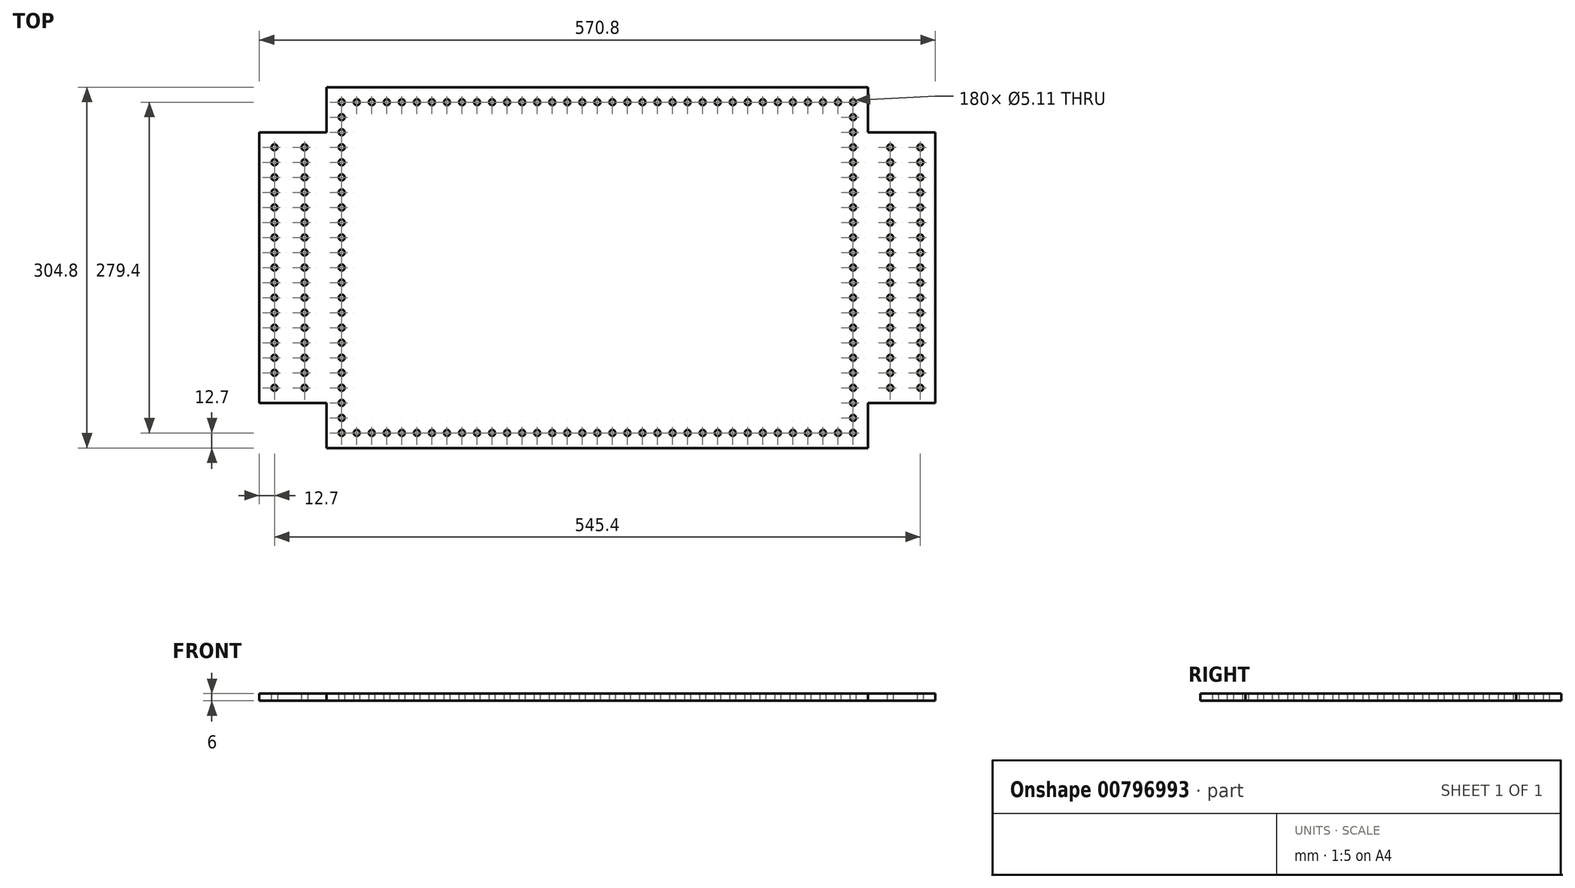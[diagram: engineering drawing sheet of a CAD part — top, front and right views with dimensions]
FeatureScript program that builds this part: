
annotation { "Feature Type Name" : "Feature", "Feature Type Description" : "" }
export const myFeature = defineFeature(function(context is Context, id is Id, definition is map)
    precondition{}
    {
        {
            var Q0;
            Q0=qCreatedBy(makeId("Top.planeOp"),FACE);
            var sketch = newSketch(context, id + "F0", { "sketchPlane" : qUnion([Q0])});
            skLineSegment(sketch, "E0.bottom", {"start": v(228.6, 152.4) * mm, "end": v(-228.6, 152.4) * mm});
            skLineSegment(sketch, "E0.top", {"start": v(228.6, -152.4) * mm, "end": v(-228.6, -152.4) * mm});
            skLineSegment(sketch, "E0.left", {"start": v(228.6, 152.4) * mm, "end": v(228.6, -152.4) * mm, "construction": true});
            skLineSegment(sketch, "E0.right", {"start": v(-228.6, 152.4) * mm, "end": v(-228.6, -152.4) * mm, "construction": true});
            skCircle(sketch, "E1", {"center": v(-215.9, 139.7) * mm, "radius": 2.55 * mm});
            skCircle(sketch, "E2.0.1.0", {"center": v(-215.9, 127) * mm, "radius": 2.55 * mm});
            skCircle(sketch, "E2.0.2.0", {"center": v(-215.9, 114.3) * mm, "radius": 2.55 * mm});
            skCircle(sketch, "E2.0.3.0", {"center": v(-215.9, 101.6) * mm, "radius": 2.55 * mm});
            skCircle(sketch, "E2.0.4.0", {"center": v(-215.9, 88.9) * mm, "radius": 2.55 * mm});
            skCircle(sketch, "E2.0.5.0", {"center": v(-215.9, 76.2) * mm, "radius": 2.55 * mm});
            skCircle(sketch, "E2.0.6.0", {"center": v(-215.9, 63.5) * mm, "radius": 2.55 * mm});
            skCircle(sketch, "E2.0.7.0", {"center": v(-215.9, 50.8) * mm, "radius": 2.55 * mm});
            skCircle(sketch, "E2.0.8.0", {"center": v(-215.9, 38.1) * mm, "radius": 2.55 * mm});
            skCircle(sketch, "E2.0.9.0", {"center": v(-215.9, 25.4) * mm, "radius": 2.55 * mm});
            skCircle(sketch, "E2.0.10.0", {"center": v(-215.9, 12.7) * mm, "radius": 2.55 * mm});
            skCircle(sketch, "E2.0.11.0", {"center": v(-215.9, 0) * mm, "radius": 2.55 * mm});
            skCircle(sketch, "E2.0.12.0", {"center": v(-215.9, -12.7) * mm, "radius": 2.55 * mm});
            skCircle(sketch, "E2.0.13.0", {"center": v(-215.9, -25.4) * mm, "radius": 2.55 * mm});
            skCircle(sketch, "E2.0.14.0", {"center": v(-215.9, -38.1) * mm, "radius": 2.55 * mm});
            skCircle(sketch, "E2.0.15.0", {"center": v(-215.9, -50.8) * mm, "radius": 2.55 * mm});
            skCircle(sketch, "E2.0.16.0", {"center": v(-215.9, -63.5) * mm, "radius": 2.55 * mm});
            skCircle(sketch, "E2.0.17.0", {"center": v(-215.9, -76.2) * mm, "radius": 2.55 * mm});
            skCircle(sketch, "E2.0.18.0", {"center": v(-215.9, -88.9) * mm, "radius": 2.55 * mm});
            skCircle(sketch, "E2.0.19.0", {"center": v(-215.9, -101.6) * mm, "radius": 2.55 * mm});
            skCircle(sketch, "E2.0.20.0", {"center": v(-215.9, -114.3) * mm, "radius": 2.55 * mm});
            skCircle(sketch, "E2.0.21.0", {"center": v(-215.9, -127) * mm, "radius": 2.55 * mm});
            skCircle(sketch, "E2.0.22.0", {"center": v(-215.9, -139.7) * mm, "radius": 2.55 * mm});
            skCircle(sketch, "E2.1.0.0", {"center": v(-203.2, 139.7) * mm, "radius": 2.55 * mm});
            skCircle(sketch, "E2.1.22.0", {"center": v(-203.2, -139.7) * mm, "radius": 2.55 * mm});
            skCircle(sketch, "E2.2.0.0", {"center": v(-190.5, 139.7) * mm, "radius": 2.55 * mm});
            skCircle(sketch, "E2.2.22.0", {"center": v(-190.5, -139.7) * mm, "radius": 2.55 * mm});
            skCircle(sketch, "E2.3.0.0", {"center": v(-177.8, 139.7) * mm, "radius": 2.55 * mm});
            skCircle(sketch, "E2.3.22.0", {"center": v(-177.8, -139.7) * mm, "radius": 2.55 * mm});
            skCircle(sketch, "E2.4.0.0", {"center": v(-165.1, 139.7) * mm, "radius": 2.55 * mm});
            skCircle(sketch, "E2.4.22.0", {"center": v(-165.1, -139.7) * mm, "radius": 2.55 * mm});
            skCircle(sketch, "E2.5.0.0", {"center": v(-152.4, 139.7) * mm, "radius": 2.55 * mm});
            skCircle(sketch, "E2.5.22.0", {"center": v(-152.4, -139.7) * mm, "radius": 2.55 * mm});
            skCircle(sketch, "E2.6.0.0", {"center": v(-139.7, 139.7) * mm, "radius": 2.55 * mm});
            skCircle(sketch, "E2.6.22.0", {"center": v(-139.7, -139.7) * mm, "radius": 2.55 * mm});
            skCircle(sketch, "E2.7.0.0", {"center": v(-127, 139.7) * mm, "radius": 2.55 * mm});
            skCircle(sketch, "E2.7.22.0", {"center": v(-127, -139.7) * mm, "radius": 2.55 * mm});
            skCircle(sketch, "E2.8.0.0", {"center": v(-114.3, 139.7) * mm, "radius": 2.55 * mm});
            skCircle(sketch, "E2.8.22.0", {"center": v(-114.3, -139.7) * mm, "radius": 2.55 * mm});
            skCircle(sketch, "E2.9.0.0", {"center": v(-101.6, 139.7) * mm, "radius": 2.55 * mm});
            skCircle(sketch, "E2.9.22.0", {"center": v(-101.6, -139.7) * mm, "radius": 2.55 * mm});
            skCircle(sketch, "E2.10.0.0", {"center": v(-88.9, 139.7) * mm, "radius": 2.55 * mm});
            skCircle(sketch, "E2.10.22.0", {"center": v(-88.9, -139.7) * mm, "radius": 2.55 * mm});
            skCircle(sketch, "E2.11.0.0", {"center": v(-76.2, 139.7) * mm, "radius": 2.55 * mm});
            skCircle(sketch, "E2.11.22.0", {"center": v(-76.2, -139.7) * mm, "radius": 2.55 * mm});
            skCircle(sketch, "E2.12.0.0", {"center": v(-63.5, 139.7) * mm, "radius": 2.55 * mm});
            skCircle(sketch, "E2.12.22.0", {"center": v(-63.5, -139.7) * mm, "radius": 2.55 * mm});
            skCircle(sketch, "E2.13.0.0", {"center": v(-50.8, 139.7) * mm, "radius": 2.55 * mm});
            skCircle(sketch, "E2.13.22.0", {"center": v(-50.8, -139.7) * mm, "radius": 2.55 * mm});
            skCircle(sketch, "E2.14.0.0", {"center": v(-38.1, 139.7) * mm, "radius": 2.55 * mm});
            skCircle(sketch, "E2.14.22.0", {"center": v(-38.1, -139.7) * mm, "radius": 2.55 * mm});
            skCircle(sketch, "E2.15.0.0", {"center": v(-25.4, 139.7) * mm, "radius": 2.55 * mm});
            skCircle(sketch, "E2.15.22.0", {"center": v(-25.4, -139.7) * mm, "radius": 2.55 * mm});
            skCircle(sketch, "E2.16.0.0", {"center": v(-12.7, 139.7) * mm, "radius": 2.55 * mm});
            skCircle(sketch, "E2.16.22.0", {"center": v(-12.7, -139.7) * mm, "radius": 2.55 * mm});
            skCircle(sketch, "E2.17.0.0", {"center": v(0, 139.7) * mm, "radius": 2.55 * mm});
            skCircle(sketch, "E2.17.22.0", {"center": v(0, -139.7) * mm, "radius": 2.55 * mm});
            skCircle(sketch, "E2.18.0.0", {"center": v(12.7, 139.7) * mm, "radius": 2.55 * mm});
            skCircle(sketch, "E2.18.22.0", {"center": v(12.7, -139.7) * mm, "radius": 2.55 * mm});
            skCircle(sketch, "E2.19.0.0", {"center": v(25.4, 139.7) * mm, "radius": 2.55 * mm});
            skCircle(sketch, "E2.19.22.0", {"center": v(25.4, -139.7) * mm, "radius": 2.55 * mm});
            skCircle(sketch, "E2.20.0.0", {"center": v(38.1, 139.7) * mm, "radius": 2.55 * mm});
            skCircle(sketch, "E2.20.22.0", {"center": v(38.1, -139.7) * mm, "radius": 2.55 * mm});
            skCircle(sketch, "E2.21.0.0", {"center": v(50.8, 139.7) * mm, "radius": 2.55 * mm});
            skCircle(sketch, "E2.21.22.0", {"center": v(50.8, -139.7) * mm, "radius": 2.55 * mm});
            skCircle(sketch, "E2.22.0.0", {"center": v(63.5, 139.7) * mm, "radius": 2.55 * mm});
            skCircle(sketch, "E2.22.22.0", {"center": v(63.5, -139.7) * mm, "radius": 2.55 * mm});
            skCircle(sketch, "E2.23.0.0", {"center": v(76.2, 139.7) * mm, "radius": 2.55 * mm});
            skCircle(sketch, "E2.23.22.0", {"center": v(76.2, -139.7) * mm, "radius": 2.55 * mm});
            skCircle(sketch, "E2.24.0.0", {"center": v(88.9, 139.7) * mm, "radius": 2.55 * mm});
            skCircle(sketch, "E2.24.22.0", {"center": v(88.9, -139.7) * mm, "radius": 2.55 * mm});
            skCircle(sketch, "E2.25.0.0", {"center": v(101.6, 139.7) * mm, "radius": 2.55 * mm});
            skCircle(sketch, "E2.25.22.0", {"center": v(101.6, -139.7) * mm, "radius": 2.55 * mm});
            skCircle(sketch, "E2.26.0.0", {"center": v(114.3, 139.7) * mm, "radius": 2.55 * mm});
            skCircle(sketch, "E2.26.22.0", {"center": v(114.3, -139.7) * mm, "radius": 2.55 * mm});
            skCircle(sketch, "E2.27.0.0", {"center": v(127, 139.7) * mm, "radius": 2.55 * mm});
            skCircle(sketch, "E2.27.22.0", {"center": v(127, -139.7) * mm, "radius": 2.55 * mm});
            skCircle(sketch, "E2.28.0.0", {"center": v(139.7, 139.7) * mm, "radius": 2.55 * mm});
            skCircle(sketch, "E2.28.22.0", {"center": v(139.7, -139.7) * mm, "radius": 2.55 * mm});
            skCircle(sketch, "E2.29.0.0", {"center": v(152.4, 139.7) * mm, "radius": 2.55 * mm});
            skCircle(sketch, "E2.29.22.0", {"center": v(152.4, -139.7) * mm, "radius": 2.55 * mm});
            skCircle(sketch, "E2.30.0.0", {"center": v(165.1, 139.7) * mm, "radius": 2.55 * mm});
            skCircle(sketch, "E2.30.22.0", {"center": v(165.1, -139.7) * mm, "radius": 2.55 * mm});
            skLineSegment(sketch, "E2.direction1", {"start": v(-215.9, 139.7) * mm, "end": v(-203.2, 139.7) * mm, "construction": true});
            skLineSegment(sketch, "E2.direction2", {"start": v(-215.9, 139.7) * mm, "end": v(-215.9, 127) * mm, "construction": true});
            skLineSegment(sketch, "E3", {"start": v(228.6, 152.4) * mm, "end": v(228.6, 114.3) * mm});
            skLineSegment(sketch, "E4", {"start": v(228.6, 114.3) * mm, "end": v(285.4, 114.3) * mm});
            skLineSegment(sketch, "E5", {"start": v(285.4, 114.3) * mm, "end": v(285.4, -114.3) * mm});
            skLineSegment(sketch, "E6", {"start": v(285.4, -114.3) * mm, "end": v(228.6, -114.3) * mm});
            skLineSegment(sketch, "E7", {"start": v(228.6, -114.3) * mm, "end": v(228.6, -152.4) * mm});
            skLineSegment(sketch, "E8", {"start": v(-228.6, -152.4) * mm, "end": v(-228.6, -114.3) * mm});
            skLineSegment(sketch, "E9", {"start": v(-228.6, -114.3) * mm, "end": v(-285.4, -114.3) * mm});
            skLineSegment(sketch, "E10", {"start": v(-285.4, -114.3) * mm, "end": v(-285.4, 114.3) * mm});
            skLineSegment(sketch, "E11", {"start": v(-285.4, 114.3) * mm, "end": v(-228.6, 114.3) * mm});
            skLineSegment(sketch, "E12", {"start": v(-228.6, 114.3) * mm, "end": v(-228.6, 152.4) * mm});
            skCircle(sketch, "E13", {"center": v(-272.7, 101.6) * mm, "radius": 2.55 * mm});
            skCircle(sketch, "E14.0.1.0", {"center": v(-272.7, 88.9) * mm, "radius": 2.55 * mm});
            skCircle(sketch, "E14.0.2.0", {"center": v(-272.7, 76.2) * mm, "radius": 2.55 * mm});
            skCircle(sketch, "E14.0.3.0", {"center": v(-272.7, 63.5) * mm, "radius": 2.55 * mm});
            skCircle(sketch, "E14.0.4.0", {"center": v(-272.7, 50.8) * mm, "radius": 2.55 * mm});
            skCircle(sketch, "E14.0.5.0", {"center": v(-272.7, 38.1) * mm, "radius": 2.55 * mm});
            skCircle(sketch, "E14.0.6.0", {"center": v(-272.7, 25.4) * mm, "radius": 2.55 * mm});
            skCircle(sketch, "E14.0.7.0", {"center": v(-272.7, 12.7) * mm, "radius": 2.55 * mm});
            skCircle(sketch, "E14.0.8.0", {"center": v(-272.7, 0) * mm, "radius": 2.55 * mm});
            skCircle(sketch, "E14.0.9.0", {"center": v(-272.7, -12.7) * mm, "radius": 2.55 * mm});
            skCircle(sketch, "E14.0.10.0", {"center": v(-272.7, -25.4) * mm, "radius": 2.55 * mm});
            skCircle(sketch, "E14.0.11.0", {"center": v(-272.7, -38.1) * mm, "radius": 2.55 * mm});
            skCircle(sketch, "E14.0.12.0", {"center": v(-272.7, -50.8) * mm, "radius": 2.55 * mm});
            skCircle(sketch, "E14.0.13.0", {"center": v(-272.7, -63.5) * mm, "radius": 2.55 * mm});
            skCircle(sketch, "E14.0.14.0", {"center": v(-272.7, -76.2) * mm, "radius": 2.55 * mm});
            skCircle(sketch, "E14.0.15.0", {"center": v(-272.7, -88.9) * mm, "radius": 2.55 * mm});
            skCircle(sketch, "E14.0.16.0", {"center": v(-272.7, -101.6) * mm, "radius": 2.55 * mm});
            skCircle(sketch, "E14.1.0.0", {"center": v(-247.3, 101.6) * mm, "radius": 2.55 * mm});
            skCircle(sketch, "E14.1.1.0", {"center": v(-247.3, 88.9) * mm, "radius": 2.55 * mm});
            skCircle(sketch, "E14.1.2.0", {"center": v(-247.3, 76.2) * mm, "radius": 2.55 * mm});
            skCircle(sketch, "E14.1.3.0", {"center": v(-247.3, 63.5) * mm, "radius": 2.55 * mm});
            skCircle(sketch, "E14.1.4.0", {"center": v(-247.3, 50.8) * mm, "radius": 2.55 * mm});
            skCircle(sketch, "E14.1.5.0", {"center": v(-247.3, 38.1) * mm, "radius": 2.55 * mm});
            skCircle(sketch, "E14.1.6.0", {"center": v(-247.3, 25.4) * mm, "radius": 2.55 * mm});
            skCircle(sketch, "E14.1.7.0", {"center": v(-247.3, 12.7) * mm, "radius": 2.55 * mm});
            skCircle(sketch, "E14.1.8.0", {"center": v(-247.3, 0) * mm, "radius": 2.55 * mm});
            skCircle(sketch, "E14.1.9.0", {"center": v(-247.3, -12.7) * mm, "radius": 2.55 * mm});
            skCircle(sketch, "E14.1.10.0", {"center": v(-247.3, -25.4) * mm, "radius": 2.55 * mm});
            skCircle(sketch, "E14.1.11.0", {"center": v(-247.3, -38.1) * mm, "radius": 2.55 * mm});
            skCircle(sketch, "E14.1.12.0", {"center": v(-247.3, -50.8) * mm, "radius": 2.55 * mm});
            skCircle(sketch, "E14.1.13.0", {"center": v(-247.3, -63.5) * mm, "radius": 2.55 * mm});
            skCircle(sketch, "E14.1.14.0", {"center": v(-247.3, -76.2) * mm, "radius": 2.55 * mm});
            skCircle(sketch, "E14.1.15.0", {"center": v(-247.3, -88.9) * mm, "radius": 2.55 * mm});
            skCircle(sketch, "E14.1.16.0", {"center": v(-247.3, -101.6) * mm, "radius": 2.55 * mm});
            skLineSegment(sketch, "E14.direction1", {"start": v(-272.7, 101.6) * mm, "end": v(-247.3, 101.6) * mm, "construction": true});
            skLineSegment(sketch, "E14.direction2", {"start": v(-272.7, 101.6) * mm, "end": v(-272.7, 88.9) * mm, "construction": true});
            skLineSegment(sketch, "E15", {"start": v(0, 152.4) * mm, "end": v(0, -152.4) * mm, "construction": true});
            skCircle(sketch, "E16.MirrorC", {"center": v(272.7, 101.6) * mm, "radius": 2.55 * mm});
            skCircle(sketch, "E17.MirrorC", {"center": v(247.3, 101.6) * mm, "radius": 2.55 * mm});
            skCircle(sketch, "E18.MirrorC", {"center": v(272.7, 88.9) * mm, "radius": 2.55 * mm});
            skCircle(sketch, "E19.MirrorC", {"center": v(247.3, -63.5) * mm, "radius": 2.55 * mm});
            skCircle(sketch, "E20.MirrorC", {"center": v(247.3, 0) * mm, "radius": 2.55 * mm});
            skCircle(sketch, "E21.MirrorC", {"center": v(272.7, 76.2) * mm, "radius": 2.55 * mm});
            skCircle(sketch, "E22.MirrorC", {"center": v(272.7, -38.1) * mm, "radius": 2.55 * mm});
            skCircle(sketch, "E23.MirrorC", {"center": v(247.3, -38.1) * mm, "radius": 2.55 * mm});
            skCircle(sketch, "E24.MirrorC", {"center": v(247.3, 50.8) * mm, "radius": 2.55 * mm});
            skCircle(sketch, "E25.MirrorC", {"center": v(272.7, -50.8) * mm, "radius": 2.55 * mm});
            skCircle(sketch, "E26.MirrorC", {"center": v(272.7, 25.4) * mm, "radius": 2.55 * mm});
            skCircle(sketch, "E27.MirrorC", {"center": v(247.3, -50.8) * mm, "radius": 2.55 * mm});
            skCircle(sketch, "E28.MirrorC", {"center": v(272.7, -76.2) * mm, "radius": 2.55 * mm});
            skCircle(sketch, "E29.MirrorC", {"center": v(272.7, 38.1) * mm, "radius": 2.55 * mm});
            skCircle(sketch, "E30.MirrorC", {"center": v(272.7, 63.5) * mm, "radius": 2.55 * mm});
            skCircle(sketch, "E31.MirrorC", {"center": v(247.3, -12.7) * mm, "radius": 2.55 * mm});
            skCircle(sketch, "E32.MirrorC", {"center": v(247.3, 12.7) * mm, "radius": 2.55 * mm});
            skCircle(sketch, "E33.MirrorC", {"center": v(272.7, -63.5) * mm, "radius": 2.55 * mm});
            skCircle(sketch, "E34.MirrorC", {"center": v(247.3, 38.1) * mm, "radius": 2.55 * mm});
            skCircle(sketch, "E35.MirrorC", {"center": v(247.3, -76.2) * mm, "radius": 2.55 * mm});
            skCircle(sketch, "E36.MirrorC", {"center": v(272.7, -25.4) * mm, "radius": 2.55 * mm});
            skCircle(sketch, "E37.MirrorC", {"center": v(247.3, 76.2) * mm, "radius": 2.55 * mm});
            skCircle(sketch, "E38.MirrorC", {"center": v(247.3, -25.4) * mm, "radius": 2.55 * mm});
            skCircle(sketch, "E39.MirrorC", {"center": v(272.7, 12.7) * mm, "radius": 2.55 * mm});
            skCircle(sketch, "E40.MirrorC", {"center": v(247.3, 88.9) * mm, "radius": 2.55 * mm});
            skCircle(sketch, "E41.MirrorC", {"center": v(272.7, 0) * mm, "radius": 2.55 * mm});
            skCircle(sketch, "E42.MirrorC", {"center": v(272.7, -12.7) * mm, "radius": 2.55 * mm});
            skCircle(sketch, "E43.MirrorC", {"center": v(272.7, 50.8) * mm, "radius": 2.55 * mm});
            skCircle(sketch, "E44.MirrorC", {"center": v(247.3, -88.9) * mm, "radius": 2.55 * mm});
            skCircle(sketch, "E45.MirrorC", {"center": v(272.7, -88.9) * mm, "radius": 2.55 * mm});
            skCircle(sketch, "E46.MirrorC", {"center": v(247.3, 25.4) * mm, "radius": 2.55 * mm});
            skCircle(sketch, "E47.MirrorC", {"center": v(247.3, 63.5) * mm, "radius": 2.55 * mm});
            skLineSegment(sketch, "E48.MirrorCS", {"start": v(272.7, 101.6) * mm, "end": v(247.3, 101.6) * mm, "construction": true});
            skLineSegment(sketch, "E49.MirrorCS", {"start": v(272.7, 101.6) * mm, "end": v(272.7, 88.9) * mm, "construction": true});
            skCircle(sketch, "E50.MirrorC", {"center": v(272.7, -101.6) * mm, "radius": 2.55 * mm});
            skCircle(sketch, "E51.MirrorC", {"center": v(247.3, -101.6) * mm, "radius": 2.55 * mm});
            skCircle(sketch, "E52.0.31.0", {"center": v(177.8, 139.7) * mm, "radius": 2.55 * mm});
            skCircle(sketch, "E52.0.31.22", {"center": v(177.8, -139.7) * mm, "radius": 2.55 * mm});
            skCircle(sketch, "E53.0.32.0", {"center": v(190.5, 139.7) * mm, "radius": 2.55 * mm});
            skCircle(sketch, "E53.0.32.22", {"center": v(190.5, -139.7) * mm, "radius": 2.55 * mm});
            skCircle(sketch, "E53.0.33.0", {"center": v(203.2, 139.7) * mm, "radius": 2.55 * mm});
            skCircle(sketch, "E53.0.33.22", {"center": v(203.2, -139.7) * mm, "radius": 2.55 * mm});
            skCircle(sketch, "E53.0.34.0", {"center": v(215.9, 139.7) * mm, "radius": 2.55 * mm});
            skCircle(sketch, "E53.0.34.1", {"center": v(215.9, 127) * mm, "radius": 2.55 * mm});
            skCircle(sketch, "E53.0.34.2", {"center": v(215.9, 114.3) * mm, "radius": 2.55 * mm});
            skCircle(sketch, "E53.0.34.3", {"center": v(215.9, 101.6) * mm, "radius": 2.55 * mm});
            skCircle(sketch, "E53.0.34.4", {"center": v(215.9, 88.9) * mm, "radius": 2.55 * mm});
            skCircle(sketch, "E53.0.34.5", {"center": v(215.9, 76.2) * mm, "radius": 2.55 * mm});
            skCircle(sketch, "E53.0.34.6", {"center": v(215.9, 63.5) * mm, "radius": 2.55 * mm});
            skCircle(sketch, "E53.0.34.7", {"center": v(215.9, 50.8) * mm, "radius": 2.55 * mm});
            skCircle(sketch, "E53.0.34.8", {"center": v(215.9, 38.1) * mm, "radius": 2.55 * mm});
            skCircle(sketch, "E53.0.34.9", {"center": v(215.9, 25.4) * mm, "radius": 2.55 * mm});
            skCircle(sketch, "E53.0.34.10", {"center": v(215.9, 12.7) * mm, "radius": 2.55 * mm});
            skCircle(sketch, "E53.0.34.11", {"center": v(215.9, 0) * mm, "radius": 2.55 * mm});
            skCircle(sketch, "E53.0.34.12", {"center": v(215.9, -12.7) * mm, "radius": 2.55 * mm});
            skCircle(sketch, "E53.0.34.13", {"center": v(215.9, -25.4) * mm, "radius": 2.55 * mm});
            skCircle(sketch, "E53.0.34.14", {"center": v(215.9, -38.1) * mm, "radius": 2.55 * mm});
            skCircle(sketch, "E53.0.34.15", {"center": v(215.9, -50.8) * mm, "radius": 2.55 * mm});
            skCircle(sketch, "E53.0.34.16", {"center": v(215.9, -63.5) * mm, "radius": 2.55 * mm});
            skCircle(sketch, "E53.0.34.17", {"center": v(215.9, -76.2) * mm, "radius": 2.55 * mm});
            skCircle(sketch, "E53.0.34.18", {"center": v(215.9, -88.9) * mm, "radius": 2.55 * mm});
            skCircle(sketch, "E53.0.34.19", {"center": v(215.9, -101.6) * mm, "radius": 2.55 * mm});
            skCircle(sketch, "E53.0.34.20", {"center": v(215.9, -114.3) * mm, "radius": 2.55 * mm});
            skCircle(sketch, "E53.0.34.21", {"center": v(215.9, -127) * mm, "radius": 2.55 * mm});
            skCircle(sketch, "E53.0.34.22", {"center": v(215.9, -139.7) * mm, "radius": 2.55 * mm});
            skSolve(sketch);
        }
        {
            var Q0;
            Q0 = qSketchRegion(id + "F0", true);
            extrude(context, id + "F1", {"entities" : qUnion([Q0]), "depth" : 6 * mm, "offsetDistance" : 25.4 * mm});
        }
    });
